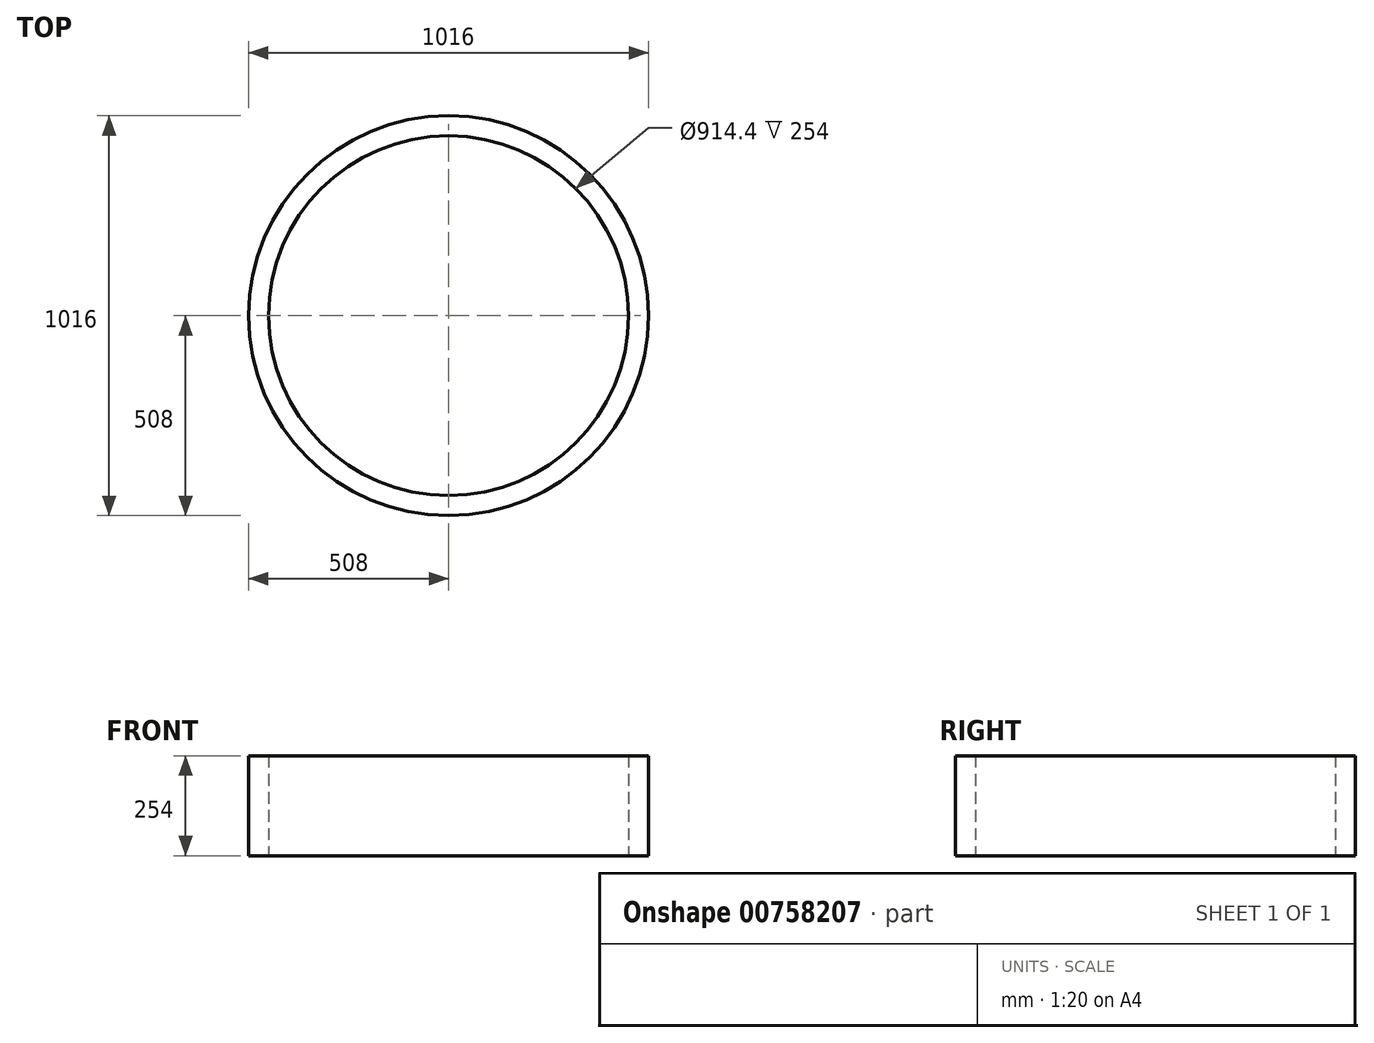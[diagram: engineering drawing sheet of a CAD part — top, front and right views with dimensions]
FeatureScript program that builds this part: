
annotation { "Feature Type Name" : "Feature", "Feature Type Description" : "" }
export const myFeature = defineFeature(function(context is Context, id is Id, definition is map)
    precondition{}
    {
        {
            var Q0;
            Q0=qCreatedBy(makeId("Top.planeOp"),FACE);
            var sketch = newSketch(context, id + "F0", { "sketchPlane" : qUnion([Q0])});
            skCircle(sketch, "E0", {"center": v(0, 0) * mm, "radius": 508 * mm});
            skCircle(sketch, "E1", {"center": v(0, 0) * mm, "radius": 457.2 * mm});
            skSolve(sketch);
        }
        {
            var Q0;
            Q0=makeQuery(id+"F0.imprint","IMPRINT",FACE,{"disambiguationData":[TD([[makeQuery(id+"F0.imprint","IMPRINT",EDGE,{"derivedFrom":sQuery(id+"F0.wireOp",EDGE,"E0")}),1.0]])]});
            extrude(context, id + "F1", {"entities" : qUnion([Q0]), "depth" : 254 * mm, "offsetDistance" : 25.4 * mm});
        }
    });
